FCSTD DOCUMENT  (FreeCAD 1.0R39319 (Git))
Label: Week1Sketch9
License: All rights reserved
LicenseURL: https://en.wikipedia.org/wiki/All_rights_reserved
objects: Sketcher::SketchObject×1, PartDesign::Body×1
note: 3 computed .brp shape members not serialized (recipe doc carries the construction recipe); baked Part::Feature solids carry a one-line shape summary decoded from their .brp

FEATURE [Sketcher::SketchObject] Sketch
  ArcFitTolerance = 1e-06
  AttachmentSupport = -> [XY_Plane]
  FullyConstrained = true
  MakeInternals = false
  MapMode = 5
  sketch-geometry (12):
    g0: Circle CenterX=0 CenterY=0 CenterZ=0 NormalX=0 NormalY=0 NormalZ=1 AngleXU=0 Radius=7.5
    g1: ArcOfCircle CenterX=0 CenterY=0 CenterZ=0 NormalX=0 NormalY=0 NormalZ=1 AngleXU=0 Radius=15 StartAngle=1.5708 EndAngle=3.14159
    g2: Circle CenterX=60 CenterY=-70 CenterZ=0 NormalX=0 NormalY=0 NormalZ=1 AngleXU=0 Radius=7.5
    g3: ArcOfCircle CenterX=60 CenterY=-70 CenterZ=0 NormalX=0 NormalY=0 NormalZ=1 AngleXU=0 Radius=20 StartAngle=4.71239 EndAngle=8.70017
    g4: LineSegment StartX=60 StartY=-90 StartZ=0 EndX=45 EndY=-90 EndZ=0
    g5: ArcOfCircle CenterX=45 CenterY=-60 CenterZ=0 NormalX=0 NormalY=0 NormalZ=1 AngleXU=0 Radius=30 StartAngle=3.14159 EndAngle=4.71239
    g6: LineSegment StartX=15 StartY=-60 StartZ=0 EndX=15 EndY=-50 EndZ=0
    g7: ArcOfCircle CenterX=5 CenterY=-50 CenterZ=0 NormalX=0 NormalY=0 NormalZ=1 AngleXU=0 Radius=10 StartAngle=0 EndAngle=1.5708
    g8: LineSegment StartX=5 StartY=-40 StartZ=0 EndX=-5 EndY=-40 EndZ=0
    g9: ArcOfCircle CenterX=-5 CenterY=-30 CenterZ=0 NormalX=0 NormalY=0 NormalZ=1 AngleXU=0 Radius=10 StartAngle=3.14159 EndAngle=4.71239
    g10: LineSegment StartX=-15 StartY=-30 StartZ=0 EndX=-15 EndY=3.6e-15 EndZ=0
    g11: ArcOfCircle CenterX=0 CenterY=-35 CenterZ=0 NormalX=0 NormalY=0 NormalZ=1 AngleXU=0 Radius=50 StartAngle=5.8333 EndAngle=7.85398
  constraints (31):
    c: Coincident(g0,g-1)
    c: Diameter(g0) = 15
    c: Radius(g1) = 15
    c: Coincident(g1,g0)
    c: PointOnObject(g1,g-1)
    c: PointOnObject(g1,g-2)
    c: Diameter(g2) = 15
    c: DistanceY(g2,g0) = 70
    c: Distance(g2,g-2) = 60
    c: Coincident(g3,g2)
    c: Diameter(g3) = 40
    c: Horizontal(g4)
    c: Tangent(g4,g5) = 1.5708
    c: Tangent(g5,g6) = 1.5708
    c: Tangent(g6,g7) = -1.5708
    c: Tangent(g7,g8) = -1.5708
    c: Tangent(g8,g9) = 1.5708
    c: Tangent(g9,g10) = 1.5708
    c: Vertical(g10)
    c: Coincident(g10,g1)
    c: Horizontal(g8)
    c: Distance(g-1,g8) = 40
    c: Radius(g9) = 10
    c: Vertical(g6)
    c: Distance(g6,g10) = 30
    c: Radius(g7) = 10
    c: Radius(g5) = 30
    c: Tangent(g1,g11) = -1.5708
    c: Radius(g11) = 50
    c: Coincident(g3,g11)
    c: Tangent(g3,g4) = 1.5708
FEATURE [PartDesign::Body] Body
  AllowCompound = false
  Group = -> [Sketch]
  Origin = -> Origin
